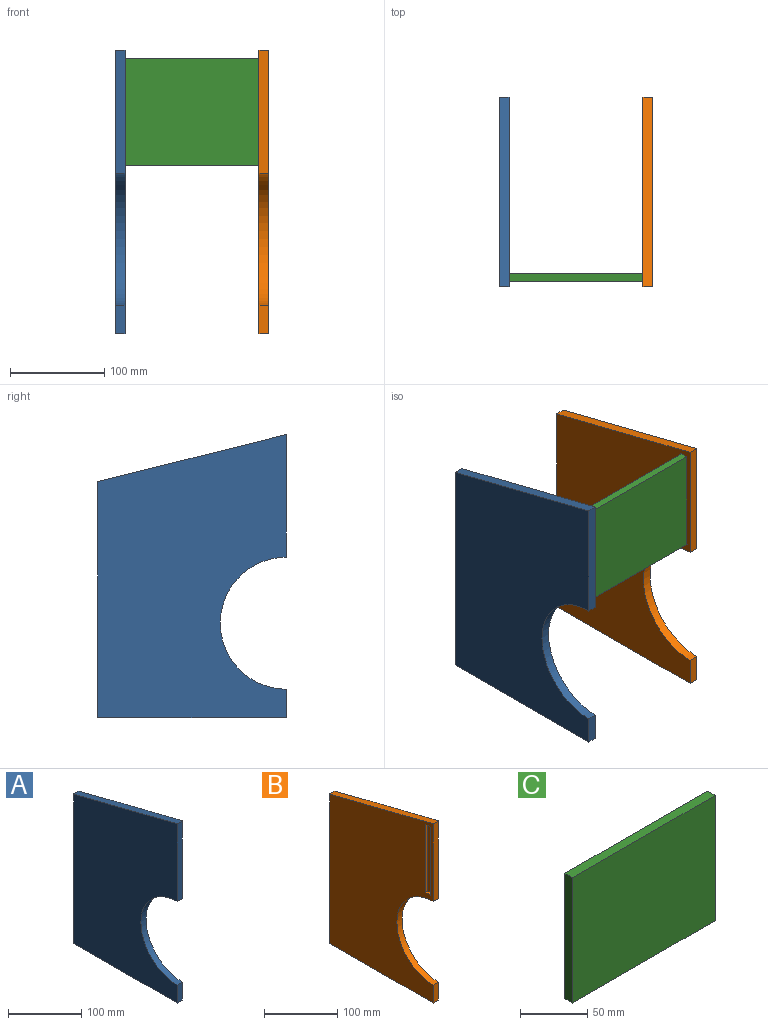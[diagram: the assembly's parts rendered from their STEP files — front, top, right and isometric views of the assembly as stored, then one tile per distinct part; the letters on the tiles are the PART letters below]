
ASSEMBLY  parts=3 mates=2
PART A: 13 faces, bbox 10x200x300 mm
  f0: plane 300x200mm, normal (1,0,0), area 46277.1mm2, adj f1,f2,f3,f4,f5,f6,f8,f9
  f1: plane 200x10mm, normal (0,0,-1), area 2000mm2, adj f0,f2,f6,f7
  f2: plane 250x10mm, normal (0,1,0), area 2500mm2, adj f0,f1,f3,f7
  f3: plane 200x50mm, normal (0,0.24,0.97), area 2061.6mm2, adj f0,f2,f4,f7
  f4: plane 130x10mm, normal (0,-1,0), area 1300mm2, adj f0,f3,f5,f7
  f5: cylinder r=70mm len=140mm, axis (-1,0,0), area 2199.1mm2, adj f0,f4,f6,f7
  f6: plane 30x10mm, normal (0,-1,0), area 300mm2, adj f0,f1,f5,f7
  f7: plane 300x200mm, normal (-1,0,0), area 47303.1mm2, adj f1,f2,f3,f4,f5,f6
  f8: plane 114x4mm, normal (0,-1,0), area 456mm2, adj f0,f9,f11,f12
  f9: plane 9x4mm, normal (0,0,-1), area 36mm2, adj f0,f8,f10,f12
  f10: plane 114x4mm, normal (0,1,0), area 456mm2, adj f0,f9,f11,f12
  f11: plane 9x4mm, normal (0,0,1), area 36mm2, adj f0,f8,f10,f12
  f12: plane 114x9mm, normal (1,0,0), area 1026mm2, adj f8,f9,f10,f11
PART B: 13 faces, bbox 10x200x300 mm
  f0: plane 300x200mm, normal (-1,0,0), area 46277.1mm2, adj f1,f2,f3,f4,f5,f6,f8,f9
  f1: plane 200x10mm, normal (0,0,-1), area 2000mm2, adj f0,f2,f6,f7
  f2: plane 250x10mm, normal (0,1,0), area 2500mm2, adj f0,f1,f3,f7
  f3: plane 200x50mm, normal (0,0.24,0.97), area 2061.6mm2, adj f0,f2,f4,f7
  f4: plane 130x10mm, normal (0,-1,0), area 1300mm2, adj f0,f3,f5,f7
  f5: cylinder r=70mm len=140mm, axis (-1,0,0), area 2199.1mm2, adj f0,f4,f6,f7
  f6: plane 30x10mm, normal (0,-1,0), area 300mm2, adj f0,f1,f5,f7
  f7: plane 300x200mm, normal (1,0,0), area 47303.1mm2, adj f1,f2,f3,f4,f5,f6
  f8: plane 114x4mm, normal (0,1,0), area 456mm2, adj f0,f9,f11,f12
  f9: plane 9x4mm, normal (0,0,-1), area 36mm2, adj f0,f8,f10,f12
  f10: plane 114x4mm, normal (0,-1,0), area 456mm2, adj f0,f9,f11,f12
  f11: plane 9x4mm, normal (0,0,1), area 36mm2, adj f0,f8,f10,f12
  f12: plane 114x9mm, normal (-1,0,0), area 1026mm2, adj f8,f9,f10,f11
PART C: 6 faces, bbox 150x8x114 mm
  f0: plane 150x8mm, normal (0,0,-1), area 1200mm2, adj f1,f3,f4,f5
  f1: plane 114x8mm, normal (1,0,0), area 912mm2, adj f0,f2,f4,f5
  f2: plane 150x8mm, normal (0,0,1), area 1200mm2, adj f1,f3,f4,f5
  f3: plane 114x8mm, normal (-1,0,0), area 912mm2, adj f0,f2,f4,f5
  f4: plane 150x114mm, normal (0,-1,0), area 17100mm2, adj f0,f1,f2,f3
  f5: plane 150x114mm, normal (0,1,0), area 17100mm2, adj f0,f1,f2,f3
PLACE A t=(-192.08,-9.23,16.54)mm
PLACE B t=(-40.08,-9.23,16.54)mm
PLACE C t=(-36.08,3.77,194.54)mm
MATE fastened C.f0 <-> A.f11  axis (0,0,1) through (-186.08,-4.23,194.54)mm
MATE fastened C.f0 <-> B.f11  axis (0,0,1) through (-36.08,-4.23,194.54)mm
